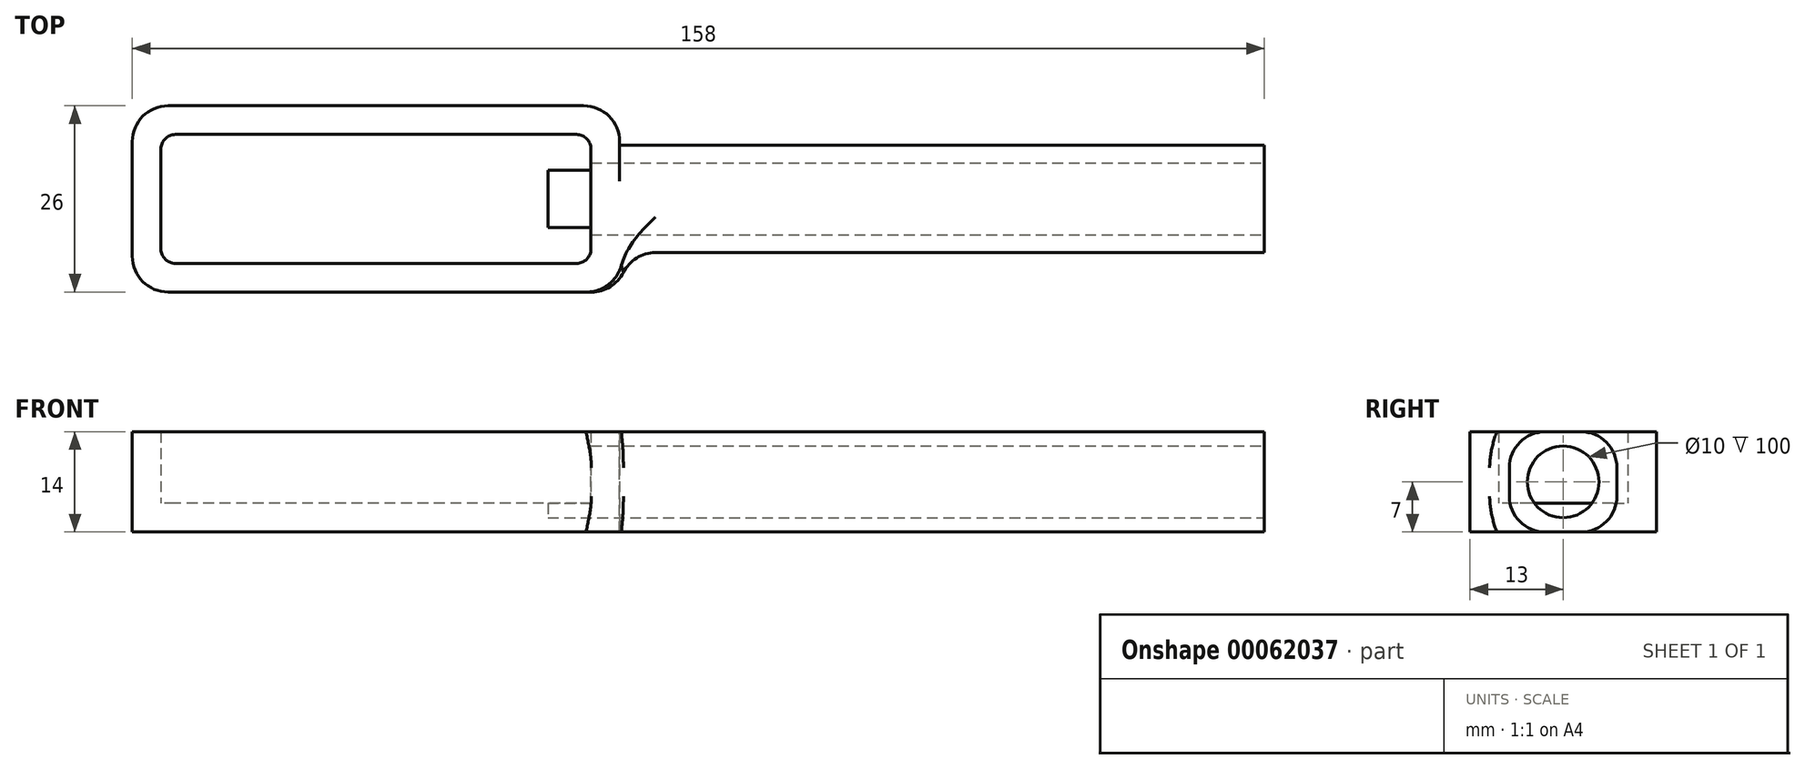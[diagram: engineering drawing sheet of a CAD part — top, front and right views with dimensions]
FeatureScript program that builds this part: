
annotation { "Feature Type Name" : "Feature", "Feature Type Description" : "" }
export const myFeature = defineFeature(function(context is Context, id is Id, definition is map)
    precondition{}
    {
        {
            var Q0;
            Q0=qCreatedBy(makeId("Top.planeOp"),FACE);
            var sketch = newSketch(context, id + "F0", { "sketchPlane" : qUnion([Q0])});
            skLineSegment(sketch, "E0.rect.bottom", {"start": v(30, 9) * mm, "end": v(-30, 9) * mm});
            skLineSegment(sketch, "E0.rect.top", {"start": v(30, -9) * mm, "end": v(-30, -9) * mm});
            skLineSegment(sketch, "E0.rect.left", {"start": v(30, 9) * mm, "end": v(30, -9) * mm});
            skLineSegment(sketch, "E0.rect.right", {"start": v(-30, 9) * mm, "end": v(-30, -9) * mm});
            skPoint(sketch, "E0.rect.middle", {"position": v(0, 0) * mm});
            skSolve(sketch);
        }
        {
            var Q0;
            Q0=makeQuery(id+"F0.imprint","IMPRINT",FACE,{"disambiguationData":[TD([[makeQuery(id+"F0.imprint","IMPRINT",EDGE,{"derivedFrom":sQuery(id+"F0.wireOp",EDGE,"E0.rect.bottom")}),1.0]])]});
            extrude(context, id + "F1", {"entities" : qUnion([Q0]), "depth" : 10 * mm});
        }
        {
            var Q0;
            Q0=makeQuery(id+"F1.opExtrude","CAP_FACE",FACE,{"disambiguationData":[OSD([sQuery(id+"F0.wireOp",EDGE,"E0.rect.bottom"),sQuery(id+"F0.wireOp",EDGE,"E0.rect.top"),sQuery(id+"F0.wireOp",EDGE,"E0.rect.left"),sQuery(id+"F0.wireOp",EDGE,"E0.rect.right")])],"isStart":false});
            shell(context, id + "F2", {"entities" : qUnion([Q0]), "thickness" : 4 * mm, "oppositeDirection" : true});
        }
        {
            var Q0;
            Q0=makeQuery(id+"F1.opExtrude","SWEPT_FACE",FACE,{"disambiguationData":[OSD([sQuery(id+"F0.wireOp",EDGE,"E0.rect.left")])]});
            var sketch = newSketch(context, id + "F3", { "sketchPlane" : qUnion([Q0])});
            skLineSegment(sketch, "E1.rect.bottom", {"start": v(7.5, -4) * mm, "end": v(-7.5, -4) * mm});
            skLineSegment(sketch, "E1.rect.top", {"start": v(7.5, 10) * mm, "end": v(-7.5, 10) * mm});
            skLineSegment(sketch, "E1.rect.left", {"start": v(7.5, -4) * mm, "end": v(7.5, 10) * mm});
            skLineSegment(sketch, "E1.rect.right", {"start": v(-7.5, -4) * mm, "end": v(-7.5, 10) * mm});
            skPoint(sketch, "E1.rect.middle", {"position": v(0, 3) * mm});
            skPoint(sketch, "E1.rect.middle.positionSnap0", {"position": v(-13, 3) * mm});
            skPoint(sketch, "E1.rect.centerSnap0", {"position": v(-13, 3) * mm});
            skSolve(sketch);
        }
        {
            var Q0;
            Q0=makeQuery(id+"F3.imprint","IMPRINT",FACE,{"disambiguationData":[TD([[makeQuery(id+"F3.imprint","IMPRINT",EDGE,{"derivedFrom":sQuery(id+"F3.wireOp",EDGE,"E1.rect.bottom")}),-1.0]])]});
            extrude(context, id + "F4", {"entities" : qUnion([Q0]), "operationType" : NewBodyOperationType.ADD, "depth" : 90 * mm});
        }
        {
            var Q0;
            Q0=makeQuery(id+"F4.opExtrude","SWEPT_EDGE",EDGE,{"disambiguationData":[OSD([sQuery(id+"F0.wireOp",EDGE,"E0.rect.left"),sQuery(id+"F3.wireOp",EDGE,"E1.rect.top"),sQuery(id+"F3.wireOp",EDGE,"E1.rect.right")])]});
            var Q1;
            Q1=makeQuery(id+"F4.opExtrude","SWEPT_EDGE",EDGE,{"disambiguationData":[OSD([sQuery(id+"F0.wireOp",EDGE,"E0.rect.left"),sQuery(id+"F3.wireOp",EDGE,"E1.rect.top"),sQuery(id+"F3.wireOp",EDGE,"E1.rect.left")])]});
            var Q2;
            Q2=makeQuery(id+"F4.opExtrude","SWEPT_EDGE",EDGE,{"disambiguationData":[OSD([sQuery(id+"F0.wireOp",EDGE,"E0.rect.left"),sQuery(id+"F3.wireOp",EDGE,"E1.rect.bottom"),sQuery(id+"F3.wireOp",EDGE,"E1.rect.right")])]});
            var Q3;
            Q3=makeQuery(id+"F4.opExtrude","SWEPT_EDGE",EDGE,{"disambiguationData":[OSD([sQuery(id+"F0.wireOp",EDGE,"E0.rect.left"),sQuery(id+"F3.wireOp",EDGE,"E1.rect.bottom"),sQuery(id+"F3.wireOp",EDGE,"E1.rect.left")])]});
            fillet(context, id + "F5", {"entities" : qUnion([Q0, Q1, Q2, Q3]), "radius" : 5 * mm, "tangentPropagation" : true, "allowEdgeOverflow" : false});
        }
        {
            var Q0;
            Q0=makeQuery(id+"F4.opExtrude","CAP_EDGE",EDGE,{"disambiguationData":[OSD([sQuery(id+"F3.wireOp",EDGE,"E1.rect.right")])],"isStart":true});
            var Q1;
            Q1=makeQuery(id+"F4.opExtrude","CAP_EDGE",EDGE,{"disambiguationData":[OSD([sQuery(id+"F3.wireOp",EDGE,"E1.rect.left")])],"isStart":true});
            fillet(context, id + "F6", {"entities" : qUnion([Q0, Q1]), "radius" : 5 * mm, "tangentPropagation" : true, "allowEdgeOverflow" : false});
        }
        {
            var Q0;
            Q0=makeQuery(id+"F1.opExtrude","SWEPT_EDGE",EDGE,{"disambiguationData":[OSD([sQuery(id+"F0.wireOp",EDGE,"E0.rect.top"),sQuery(id+"F0.wireOp",EDGE,"E0.rect.left")])]});
            var Q1;
            Q1=makeQuery(id+"F1.opExtrude","SWEPT_EDGE",EDGE,{"disambiguationData":[OSD([sQuery(id+"F0.wireOp",EDGE,"E0.rect.bottom"),sQuery(id+"F0.wireOp",EDGE,"E0.rect.left")])]});
            var Q2;
            Q2=makeQuery(id+"F1.opExtrude","SWEPT_EDGE",EDGE,{"disambiguationData":[OSD([sQuery(id+"F0.wireOp",EDGE,"E0.rect.top"),sQuery(id+"F0.wireOp",EDGE,"E0.rect.right")])]});
            var Q3;
            Q3=makeQuery(id+"F1.opExtrude","SWEPT_EDGE",EDGE,{"disambiguationData":[OSD([sQuery(id+"F0.wireOp",EDGE,"E0.rect.bottom"),sQuery(id+"F0.wireOp",EDGE,"E0.rect.right")])]});
            fillet(context, id + "F7", {"entities" : qUnion([Q0, Q1, Q2, Q3]), "radius" : 5 * mm, "tangentPropagation" : true, "allowEdgeOverflow" : false});
        }
        {
            var Q0;
            Q0=makeQuery(id+"F2.opShell","OFFSET_EDGE",EDGE,{"disambiguationData":[OSD([sQuery(id+"F0.wireOp",EDGE,"E0.rect.bottom"),sQuery(id+"F0.wireOp",EDGE,"E0.rect.right")])]});
            var Q1;
            Q1=makeQuery(id+"F2.opShell","OFFSET_EDGE",EDGE,{"disambiguationData":[OSD([sQuery(id+"F0.wireOp",EDGE,"E0.rect.top"),sQuery(id+"F0.wireOp",EDGE,"E0.rect.right")])]});
            var Q2;
            Q2=makeQuery(id+"F2.opShell","OFFSET_EDGE",EDGE,{"disambiguationData":[OSD([sQuery(id+"F0.wireOp",EDGE,"E0.rect.top"),sQuery(id+"F0.wireOp",EDGE,"E0.rect.left")])]});
            var Q3;
            Q3=makeQuery(id+"F2.opShell","OFFSET_EDGE",EDGE,{"disambiguationData":[OSD([sQuery(id+"F0.wireOp",EDGE,"E0.rect.bottom"),sQuery(id+"F0.wireOp",EDGE,"E0.rect.left")])]});
            fillet(context, id + "F8", {"entities" : qUnion([Q0, Q1, Q2, Q3]), "radius" : 2 * mm, "tangentPropagation" : true, "allowEdgeOverflow" : false});
        }
        {
            var Q0;
            Q0=makeQuery(id+"F4.opExtrude","CAP_FACE",FACE,{"disambiguationData":[OSD([sQuery(id+"F3.wireOp",EDGE,"E1.rect.bottom"),sQuery(id+"F3.wireOp",EDGE,"E1.rect.top"),sQuery(id+"F3.wireOp",EDGE,"E1.rect.left"),sQuery(id+"F3.wireOp",EDGE,"E1.rect.right")])],"isStart":false});
            var sketch = newSketch(context, id + "F9", { "sketchPlane" : qUnion([Q0])});
            skCircle(sketch, "E2", {"center": v(0, 3) * mm, "radius": 5 * mm});
            skPoint(sketch, "E2.centerSnap0", {"position": v(-7.5, 3) * mm});
            skSolve(sketch);
        }
        {
            var Q0;
            Q0=makeQuery(id+"F9.imprint","IMPRINT",FACE,{"disambiguationData":[TD([[makeQuery(id+"F9.imprint","IMPRINT",EDGE,{"derivedFrom":sQuery(id+"F9.wireOp",EDGE,"E2")}),1.0]])]});
            extrude(context, id + "F10", {"entities" : qUnion([Q0]), "operationType" : NewBodyOperationType.REMOVE, "oppositeDirection" : true, "depth" : 100 * mm});
        }
    });
